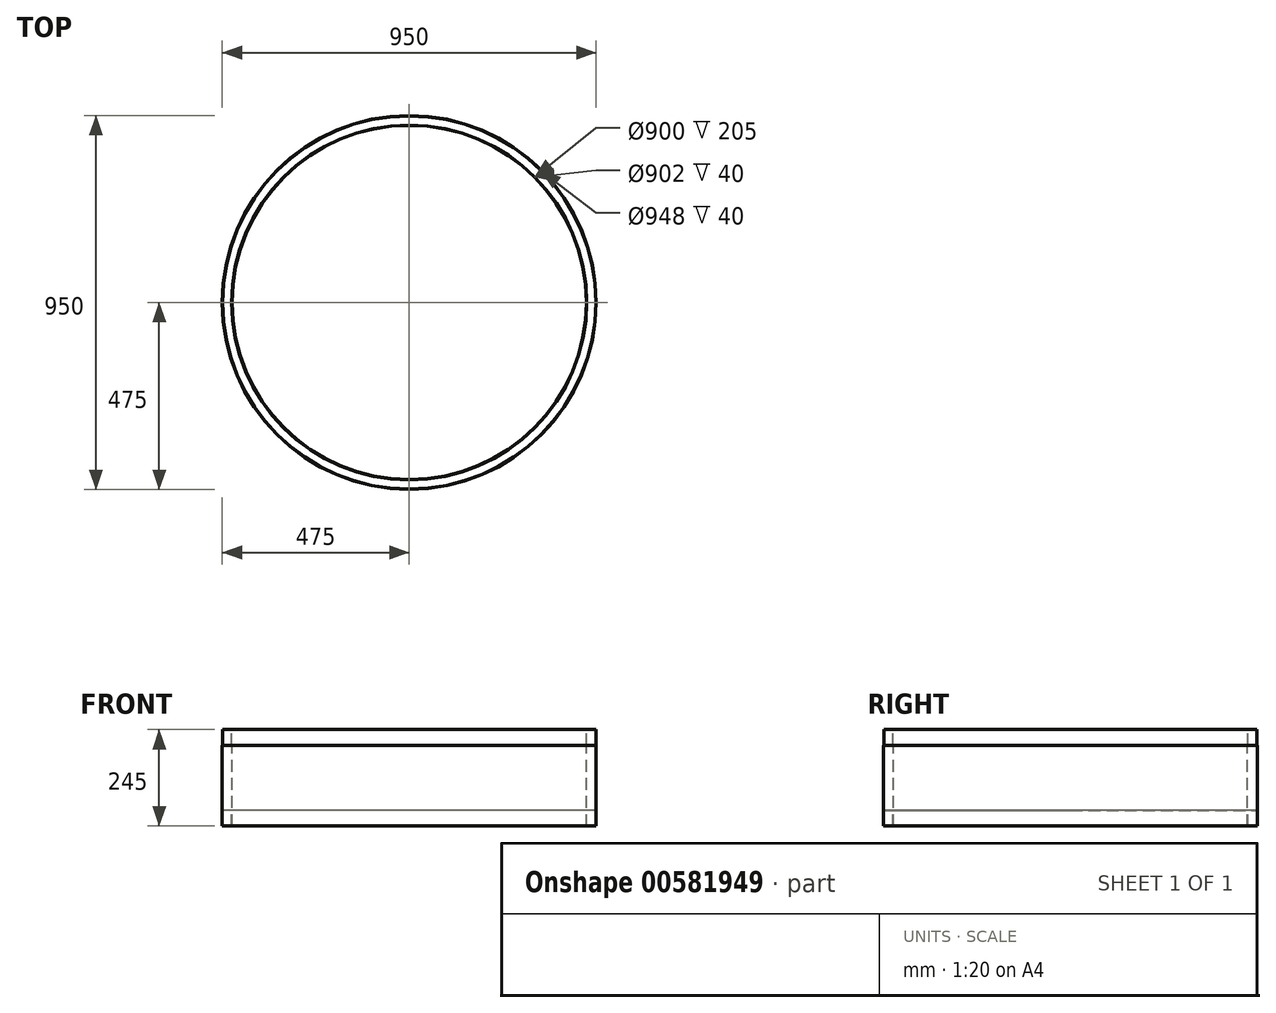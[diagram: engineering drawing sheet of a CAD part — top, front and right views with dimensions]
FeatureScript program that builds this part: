
annotation { "Feature Type Name" : "Feature", "Feature Type Description" : "" }
export const myFeature = defineFeature(function(context is Context, id is Id, definition is map)
    precondition{}
    {
        {
            var Q0;
            Q0=qCreatedBy(makeId("Front.planeOp"),FACE);
            var sketch = newSketch(context, id + "F0", { "sketchPlane" : qUnion([Q0])});
            skLineSegment(sketch, "E0", {"start": v(0, 345.75) * mm, "end": v(0, -558.03) * mm, "construction": true});
            skLineSegment(sketch, "E1", {"start": v(-450, -518.84) * mm, "end": v(-450, -313.84) * mm});
            skLineSegment(sketch, "E2", {"start": v(-450, -313.84) * mm, "end": v(-451, -313.84) * mm});
            skLineSegment(sketch, "E3", {"start": v(-451, -313.84) * mm, "end": v(-451, -273.84) * mm});
            skLineSegment(sketch, "E4", {"start": v(-451, -273.84) * mm, "end": v(-474, -273.84) * mm});
            skLineSegment(sketch, "E5", {"start": v(-474, -273.84) * mm, "end": v(-474, -313.84) * mm});
            skLineSegment(sketch, "E6", {"start": v(-474, -313.84) * mm, "end": v(-475, -313.84) * mm});
            skLineSegment(sketch, "E7", {"start": v(-475, -313.84) * mm, "end": v(-475, -518.84) * mm});
            skLineSegment(sketch, "E8", {"start": v(-475, -518.84) * mm, "end": v(-474, -518.84) * mm});
            skLineSegment(sketch, "E9", {"start": v(-474, -518.84) * mm, "end": v(-474, -478.84) * mm});
            skLineSegment(sketch, "E10", {"start": v(-474, -478.84) * mm, "end": v(-451, -478.84) * mm});
            skLineSegment(sketch, "E11", {"start": v(-451, -478.84) * mm, "end": v(-451, -518.84) * mm});
            skLineSegment(sketch, "E12", {"start": v(-451, -518.84) * mm, "end": v(-450, -518.84) * mm});
            skSolve(sketch);
        }
        {
            var Q0;
            Q0=qSketchRegion(id+"F0",true);
            var Q1;
            Q1=sQuery(id+"F0.wireOp",EDGE,"E0");
            revolve(context, id + "F1", {"entities" : qUnion([Q0]), "axis" : qUnion([Q1]), "revolveType" : RevolveType.FULL});
        }
    });
